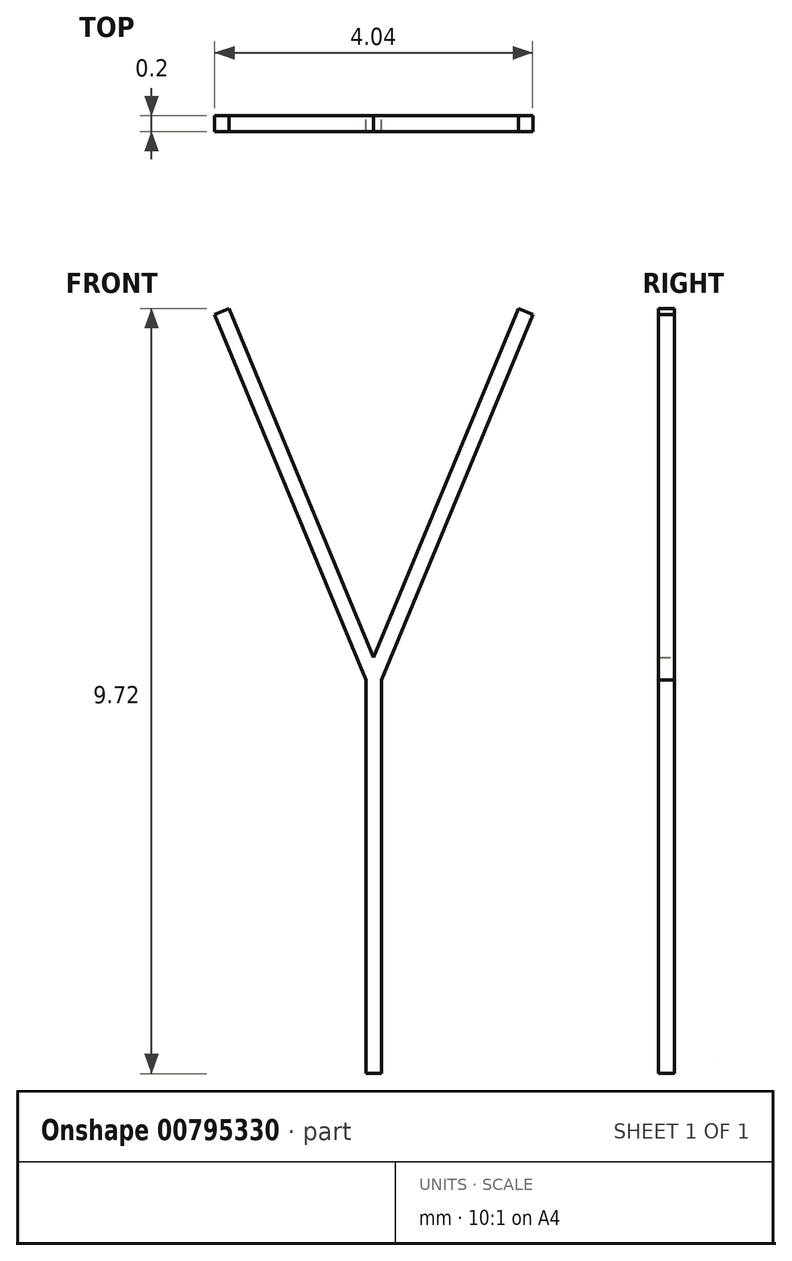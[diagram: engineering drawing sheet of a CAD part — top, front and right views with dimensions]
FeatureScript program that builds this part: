
annotation { "Feature Type Name" : "Feature", "Feature Type Description" : "" }
export const myFeature = defineFeature(function(context is Context, id is Id, definition is map)
    precondition{}
    {
        {
            var Q0;
            Q0=qCreatedBy(makeId("Front.planeOp"),FACE);
            var sketch = newSketch(context, id + "F0", { "sketchPlane" : qUnion([Q0])});
            skLineSegment(sketch, "E0", {"start": v(-2.02, 4.55) * mm, "end": v(-0.1, -0.09) * mm});
            skLineSegment(sketch, "E1", {"start": v(0.1, -0.09) * mm, "end": v(2.02, 4.55) * mm});
            skLineSegment(sketch, "E2.0", {"start": v(-1.84, 4.63) * mm, "end": v(0, 0.2) * mm});
            skLineSegment(sketch, "E3.0", {"start": v(0, 0.2) * mm, "end": v(1.84, 4.63) * mm});
            skLineSegment(sketch, "E4.0", {"start": v(0.1, -0.09) * mm, "end": v(0.1, -5.09) * mm});
            skLineSegment(sketch, "E5.0", {"start": v(-0.1, -0.09) * mm, "end": v(-0.1, -5.09) * mm});
            skLineSegment(sketch, "E6", {"start": v(-0.1, -5.09) * mm, "end": v(0.1, -5.09) * mm});
            skLineSegment(sketch, "E7", {"start": v(-1.84, 4.63) * mm, "end": v(-2.02, 4.55) * mm});
            skLineSegment(sketch, "E8", {"start": v(2.02, 4.55) * mm, "end": v(1.84, 4.63) * mm});
            skSolve(sketch);
        }
        {
            var Q0;
            Q0=qSketchRegion(id+"F0",true);
            extrude(context, id + "F1", {"entities" : qUnion([Q0]), "depth" : 0.2 * mm, "offsetDistance" : 25 * mm});
        }
    });
